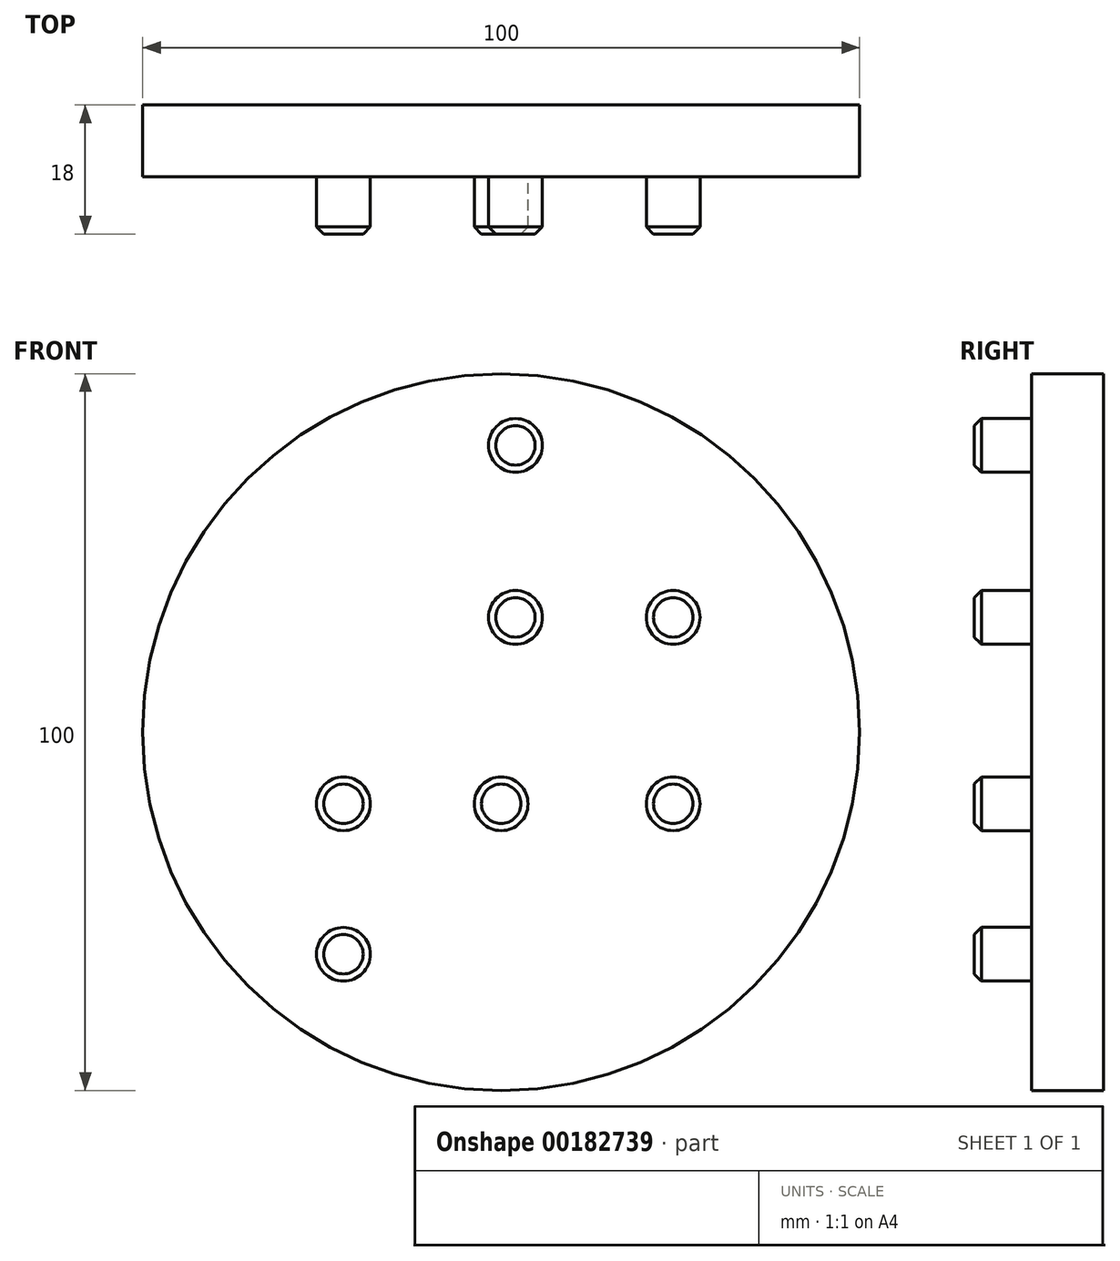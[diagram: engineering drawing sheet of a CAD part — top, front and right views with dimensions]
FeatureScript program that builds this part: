
annotation { "Feature Type Name" : "Feature", "Feature Type Description" : "" }
export const myFeature = defineFeature(function(context is Context, id is Id, definition is map)
    precondition{}
    {
        {
            var Q0;
            Q0=qCreatedBy(makeId("Front.planeOp"),FACE);
            var sketch = newSketch(context, id + "F0", { "sketchPlane" : qUnion([Q0])});
            skCircle(sketch, "E0", {"center": v(0, 0) * mm, "radius": 50 * mm});
            skSolve(sketch);
        }
        {
            var Q0;
            Q0=makeQuery(id+"F0.imprint","IMPRINT",FACE,{"disambiguationData":[TD([[makeQuery(id+"F0.imprint","IMPRINT",EDGE,{"derivedFrom":sQuery(id+"F0.wireOp",EDGE,"E0")}),1.0]])]});
            extrude(context, id + "F1", {"entities" : qUnion([Q0]), "depth" : 10 * mm});
        }
        {
            var Q0;
            Q0=makeQuery(id+"F1.opExtrude","CAP_FACE",FACE,{"disambiguationData":[OSD([sQuery(id+"F0.wireOp",EDGE,"E0")])],"isStart":false});
            var sketch = newSketch(context, id + "F2", { "sketchPlane" : qUnion([Q0])});
            skCircle(sketch, "E1", {"center": v(2, 40) * mm, "radius": 3.75 * mm});
            skCircle(sketch, "E2", {"center": v(2, 16) * mm, "radius": 3.75 * mm});
            skCircle(sketch, "E3", {"center": v(24, 16) * mm, "radius": 3.75 * mm});
            skCircle(sketch, "E4", {"center": v(24, -10) * mm, "radius": 3.75 * mm});
            skCircle(sketch, "E5", {"center": v(0, -10) * mm, "radius": 3.75 * mm});
            skCircle(sketch, "E6", {"center": v(-22, -10) * mm, "radius": 3.75 * mm});
            skCircle(sketch, "E7", {"center": v(-22, -31) * mm, "radius": 3.75 * mm});
            skSolve(sketch);
        }
        {
            var Q0;
            Q0=makeQuery(id+"F2.imprint","IMPRINT",FACE,{"disambiguationData":[TD([[makeQuery(id+"F2.imprint","IMPRINT",EDGE,{"derivedFrom":sQuery(id+"F2.wireOp",EDGE,"E1")}),1.0]])]});
            var Q1;
            Q1=makeQuery(id+"F2.imprint","IMPRINT",FACE,{"disambiguationData":[TD([[makeQuery(id+"F2.imprint","IMPRINT",EDGE,{"derivedFrom":sQuery(id+"F2.wireOp",EDGE,"E2")}),1.0]])]});
            var Q2;
            Q2=makeQuery(id+"F2.imprint","IMPRINT",FACE,{"disambiguationData":[TD([[makeQuery(id+"F2.imprint","IMPRINT",EDGE,{"derivedFrom":sQuery(id+"F2.wireOp",EDGE,"E3")}),1.0]])]});
            var Q3;
            Q3=makeQuery(id+"F2.imprint","IMPRINT",FACE,{"disambiguationData":[TD([[makeQuery(id+"F2.imprint","IMPRINT",EDGE,{"derivedFrom":sQuery(id+"F2.wireOp",EDGE,"E4")}),1.0]])]});
            var Q4;
            Q4=makeQuery(id+"F2.imprint","IMPRINT",FACE,{"disambiguationData":[TD([[makeQuery(id+"F2.imprint","IMPRINT",EDGE,{"derivedFrom":sQuery(id+"F2.wireOp",EDGE,"E5")}),1.0]])]});
            var Q5;
            Q5=makeQuery(id+"F2.imprint","IMPRINT",FACE,{"disambiguationData":[TD([[makeQuery(id+"F2.imprint","IMPRINT",EDGE,{"derivedFrom":sQuery(id+"F2.wireOp",EDGE,"E6")}),1.0]])]});
            var Q6;
            Q6=makeQuery(id+"F2.imprint","IMPRINT",FACE,{"disambiguationData":[TD([[makeQuery(id+"F2.imprint","IMPRINT",EDGE,{"derivedFrom":sQuery(id+"F2.wireOp",EDGE,"E7")}),1.0]])]});
            extrude(context, id + "F3", {"entities" : qUnion([Q0, Q1, Q2, Q3, Q4, Q5, Q6]), "operationType" : NewBodyOperationType.ADD, "depth" : 8 * mm});
        }
        {
            var Q0;
            Q0=makeQuery(id+"F3.opExtrude","CAP_EDGE",EDGE,{"disambiguationData":[OSD([sQuery(id+"F2.wireOp",EDGE,"E1")])],"isStart":false});
            var Q1;
            Q1=makeQuery(id+"F3.opExtrude","CAP_EDGE",EDGE,{"disambiguationData":[OSD([sQuery(id+"F2.wireOp",EDGE,"E2")])],"isStart":false});
            var Q2;
            Q2=makeQuery(id+"F3.opExtrude","CAP_EDGE",EDGE,{"disambiguationData":[OSD([sQuery(id+"F2.wireOp",EDGE,"E3")])],"isStart":false});
            var Q3;
            Q3=makeQuery(id+"F3.opExtrude","CAP_EDGE",EDGE,{"disambiguationData":[OSD([sQuery(id+"F2.wireOp",EDGE,"E4")])],"isStart":false});
            var Q4;
            Q4=makeQuery(id+"F3.opExtrude","CAP_EDGE",EDGE,{"disambiguationData":[OSD([sQuery(id+"F2.wireOp",EDGE,"E5")])],"isStart":false});
            var Q5;
            Q5=makeQuery(id+"F3.opExtrude","CAP_EDGE",EDGE,{"disambiguationData":[OSD([sQuery(id+"F2.wireOp",EDGE,"E6")])],"isStart":false});
            var Q6;
            Q6=makeQuery(id+"F3.opExtrude","CAP_EDGE",EDGE,{"disambiguationData":[OSD([sQuery(id+"F2.wireOp",EDGE,"E7")])],"isStart":false});
            chamfer(context, id + "F4", {"entities" : qUnion([Q0, Q1, Q2, Q3, Q4, Q5, Q6]), "width" : 1 * mm, "tangentPropagation" : true});
        }
    });
